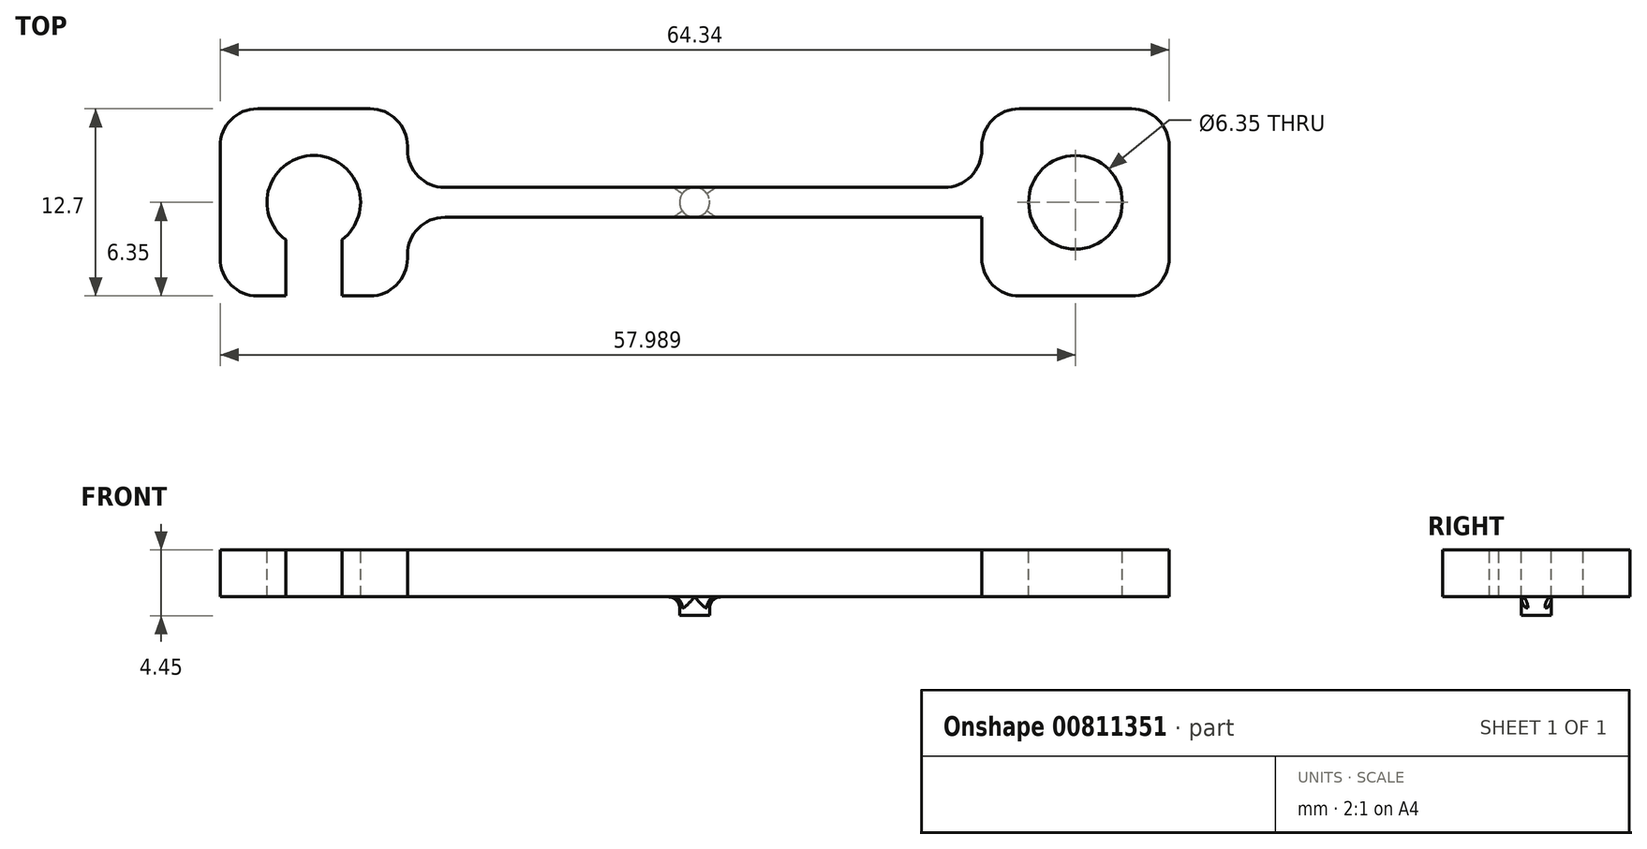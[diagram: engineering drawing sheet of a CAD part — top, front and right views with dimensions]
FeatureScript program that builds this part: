
annotation { "Feature Type Name" : "Feature", "Feature Type Description" : "" }
export const myFeature = defineFeature(function(context is Context, id is Id, definition is map)
    precondition{}
    {
        {
            var Q0;
            Q0=qCreatedBy(makeId("Top.planeOp"),FACE);
            var sketch = newSketch(context, id + "F0", { "sketchPlane" : qUnion([Q0])});
            skLineSegment(sketch, "E0.bottom", {"start": v(32.17, -6.35) * mm, "end": v(19.47, -6.35) * mm});
            skLineSegment(sketch, "E0.top", {"start": v(32.17, 6.35) * mm, "end": v(19.47, 6.35) * mm});
            skLineSegment(sketch, "E0.left", {"start": v(32.17, -6.35) * mm, "end": v(32.17, 6.35) * mm});
            skLineSegment(sketch, "E0.right", {"start": v(-32.17, -6.35) * mm, "end": v(-32.17, 6.35) * mm});
            skPoint(sketch, "E0.middle", {"position": v(0, 0) * mm});
            skLineSegment(sketch, "E1", {"start": v(-19.47, -6.35) * mm, "end": v(-19.47, -1.02) * mm});
            skLineSegment(sketch, "E2", {"start": v(-19.47, -1.02) * mm, "end": v(19.47, -1.02) * mm});
            skLineSegment(sketch, "E3", {"start": v(19.47, -1.02) * mm, "end": v(19.47, -6.35) * mm});
            skLineSegment(sketch, "E4", {"start": v(-19.47, 6.35) * mm, "end": v(-19.47, 1.02) * mm});
            skLineSegment(sketch, "E5", {"start": v(-19.47, 1.02) * mm, "end": v(19.47, 1.02) * mm});
            skLineSegment(sketch, "E6", {"start": v(19.47, 1.02) * mm, "end": v(19.47, 6.35) * mm});
            skLineSegment(sketch, "E7", {"start": v(-32.17, 0) * mm, "end": v(32.17, 0) * mm, "construction": true});
            skLineSegment(sketch, "E8", {"start": v(0, 6.35) * mm, "end": v(0, -6.35) * mm, "construction": true});
            skLineSegment(sketch, "E9.trimOffspring", {"start": v(-19.47, 6.35) * mm, "end": v(-32.17, 6.35) * mm});
            skLineSegment(sketch, "E10.trimOffspring", {"start": v(-19.47, -6.35) * mm, "end": v(-32.17, -6.35) * mm});
            skSolve(sketch);
        }
        {
            var Q0;
            Q0=makeQuery(id+"F0.imprint","IMPRINT",FACE,{"disambiguationData":[TD([[makeQuery(id+"F0.imprint","IMPRINT",EDGE,{"derivedFrom":sQuery(id+"F0.wireOp",EDGE,"E0.bottom")}),-1.0]])]});
            extrude(context, id + "F1", {"entities" : qUnion([Q0]), "oppositeDirection" : true, "depth" : 3.17 * mm, "offsetDistance" : 25.4 * mm});
        }
        {
            var Q0;
            Q0=makeQuery(id+"F1.opExtrude","CAP_FACE",FACE,{"disambiguationData":[OSD([sQuery(id+"F0.wireOp",EDGE,"E0.bottom"),sQuery(id+"F0.wireOp",EDGE,"E0.top"),sQuery(id+"F0.wireOp",EDGE,"E0.left"),sQuery(id+"F0.wireOp",EDGE,"E0.right"),sQuery(id+"F0.wireOp",EDGE,"E1"),sQuery(id+"F0.wireOp",EDGE,"E2"),sQuery(id+"F0.wireOp",EDGE,"E3"),sQuery(id+"F0.wireOp",EDGE,"E4"),sQuery(id+"F0.wireOp",EDGE,"E5"),sQuery(id+"F0.wireOp",EDGE,"E6"),sQuery(id+"F0.wireOp",EDGE,"E9.trimOffspring"),sQuery(id+"F0.wireOp",EDGE,"E10.trimOffspring")])],"isStart":true});
            var sketch = newSketch(context, id + "F2", { "sketchPlane" : qUnion([Q0])});
            skLineSegment(sketch, "E11", {"start": v(0, 1.02) * mm, "end": v(0, -1.02) * mm, "construction": true});
            skCircle(sketch, "E12", {"center": v(-25.82, 0) * mm, "radius": 3.18 * mm});
            skCircle(sketch, "E13", {"center": v(25.82, 0) * mm, "radius": 3.18 * mm});
            skLineSegment(sketch, "E14", {"start": v(-25.82, 6.35) * mm, "end": v(-25.82, -6.35) * mm, "construction": true});
            skSolve(sketch);
        }
        {
            var Q0;
            Q0=makeQuery(id+"F2.imprint","IMPRINT",FACE,{"disambiguationData":[TD([[makeQuery(id+"F2.imprint","IMPRINT",EDGE,{"derivedFrom":sQuery(id+"F2.wireOp",EDGE,"E12")}),1.0]])]});
            var Q1;
            Q1=makeQuery(id+"F2.imprint","IMPRINT",FACE,{"disambiguationData":[TD([[makeQuery(id+"F2.imprint","IMPRINT",EDGE,{"derivedFrom":sQuery(id+"F2.wireOp",EDGE,"E13")}),1.0]])]});
            extrude(context, id + "F3", {"entities" : qUnion([Q0, Q1]), "operationType" : NewBodyOperationType.REMOVE, "endBound" : BoundingType.THROUGH_ALL, "oppositeDirection" : true, "depth" : 25.4 * mm, "offsetDistance" : 25.4 * mm});
        }
        {
            var Q0;
            Q0=makeQuery(id+"F1.opExtrude","CAP_FACE",FACE,{"disambiguationData":[OSD([sQuery(id+"F0.wireOp",EDGE,"E0.bottom"),sQuery(id+"F0.wireOp",EDGE,"E0.top"),sQuery(id+"F0.wireOp",EDGE,"E0.left"),sQuery(id+"F0.wireOp",EDGE,"E0.right"),sQuery(id+"F0.wireOp",EDGE,"E1"),sQuery(id+"F0.wireOp",EDGE,"E2"),sQuery(id+"F0.wireOp",EDGE,"E3"),sQuery(id+"F0.wireOp",EDGE,"E4"),sQuery(id+"F0.wireOp",EDGE,"E5"),sQuery(id+"F0.wireOp",EDGE,"E6"),sQuery(id+"F0.wireOp",EDGE,"E9.trimOffspring"),sQuery(id+"F0.wireOp",EDGE,"E10.trimOffspring")])],"isStart":true});
            var sketch = newSketch(context, id + "F4", { "sketchPlane" : qUnion([Q0])});
            skLineSegment(sketch, "E15", {"start": v(-25.82, 6.35) * mm, "end": v(-25.82, -6.35) * mm, "construction": true});
            skLineSegment(sketch, "E16", {"start": v(-29, 0) * mm, "end": v(-22.64, 0) * mm, "construction": true});
            skLineSegment(sketch, "E17.bottom", {"start": v(-27.72, -6.35) * mm, "end": v(-23.91, -6.35) * mm});
            skLineSegment(sketch, "E17.top", {"start": v(-27.72, 0) * mm, "end": v(-23.91, 0) * mm});
            skLineSegment(sketch, "E17.left", {"start": v(-27.72, -6.35) * mm, "end": v(-27.72, 0) * mm});
            skLineSegment(sketch, "E17.right", {"start": v(-23.91, -6.35) * mm, "end": v(-23.91, 0) * mm});
            skSolve(sketch);
        }
        {
            var Q0;
            {var subQ0=sQuery(id+"F4.wireOp",EDGE,"E17.bottom");Q0=makeQuery(id+"F4.imprint","IMPRINT",FACE,{"disambiguationData":[TD([[makeQuery(id+"F4.imprint","IMPRINT",EDGE,{"derivedFrom":subQ0}),-1.0]])]});}
            extrude(context, id + "F5", {"entities" : qUnion([Q0]), "operationType" : NewBodyOperationType.REMOVE, "endBound" : BoundingType.THROUGH_ALL, "oppositeDirection" : true, "depth" : 25.4 * mm, "offsetDistance" : 25.4 * mm});
        }
        {
            var Q0;
            Q0=makeQuery(id+"F1.opExtrude","CAP_FACE",FACE,{"disambiguationData":[OSD([sQuery(id+"F0.wireOp",EDGE,"E0.bottom"),sQuery(id+"F0.wireOp",EDGE,"E0.top"),sQuery(id+"F0.wireOp",EDGE,"E0.left"),sQuery(id+"F0.wireOp",EDGE,"E0.right"),sQuery(id+"F0.wireOp",EDGE,"E1"),sQuery(id+"F0.wireOp",EDGE,"E2"),sQuery(id+"F0.wireOp",EDGE,"E3"),sQuery(id+"F0.wireOp",EDGE,"E4"),sQuery(id+"F0.wireOp",EDGE,"E5"),sQuery(id+"F0.wireOp",EDGE,"E6"),sQuery(id+"F0.wireOp",EDGE,"E9.trimOffspring"),sQuery(id+"F0.wireOp",EDGE,"E10.trimOffspring")])],"isStart":false});
            var sketch = newSketch(context, id + "F6", { "sketchPlane" : qUnion([Q0])});
            skCircle(sketch, "E18", {"center": v(0, 0) * mm, "radius": 1.02 * mm});
            skSolve(sketch);
        }
        {
            var Q0;
            Q0 = qSketchRegion(id + "F6", true);
            extrude(context, id + "F7", {"entities" : qUnion([Q0]), "operationType" : NewBodyOperationType.ADD, "depth" : 1.27 * mm, "offsetDistance" : 25.4 * mm});
        }
        {
            var Q0;
            Q0=makeQuery(id+"F7.boolean.opBoolean","SPLIT",EDGE,{"disambiguationData":[OD(1.0)],"derivedFrom":makeQuery(id+"F7.opExtrude","CAP_EDGE",EDGE,{"disambiguationData":[OSD([sQuery(id+"F6.wireOp",EDGE,"E18")])],"isStart":true})});
            var Q1;
            Q1=makeQuery(id+"F7.boolean.opBoolean","SPLIT",EDGE,{"disambiguationData":[OD(0.0)],"derivedFrom":makeQuery(id+"F7.opExtrude","CAP_EDGE",EDGE,{"disambiguationData":[OSD([sQuery(id+"F6.wireOp",EDGE,"E18")])],"isStart":true})});
            fillet(context, id + "F8", {"entities" : qUnion([Q0, Q1]), "radius" : 0.76 * mm, "tangentPropagation" : true, "allowEdgeOverflow" : false});
        }
        {
            var Q0;
            Q0=makeQuery(id+"F1.opExtrude","SWEPT_EDGE",EDGE,{"disambiguationData":[OSD([sQuery(id+"F0.wireOp",EDGE,"E1"),sQuery(id+"F0.wireOp",EDGE,"E2")])]});
            var Q1;
            Q1=makeQuery(id+"F1.opExtrude","SWEPT_EDGE",EDGE,{"disambiguationData":[OSD([sQuery(id+"F0.wireOp",EDGE,"E1"),sQuery(id+"F0.wireOp",EDGE,"E10.trimOffspring")])]});
            var Q2;
            Q2=makeQuery(id+"F1.opExtrude","SWEPT_EDGE",EDGE,{"disambiguationData":[OSD([sQuery(id+"F0.wireOp",EDGE,"E0.right"),sQuery(id+"F0.wireOp",EDGE,"E10.trimOffspring")])]});
            var Q3;
            Q3=makeQuery(id+"F1.opExtrude","SWEPT_EDGE",EDGE,{"disambiguationData":[OSD([sQuery(id+"F0.wireOp",EDGE,"E0.right"),sQuery(id+"F0.wireOp",EDGE,"E9.trimOffspring")])]});
            var Q4;
            Q4=makeQuery(id+"F1.opExtrude","SWEPT_EDGE",EDGE,{"disambiguationData":[OSD([sQuery(id+"F0.wireOp",EDGE,"E4"),sQuery(id+"F0.wireOp",EDGE,"E9.trimOffspring")])]});
            var Q5;
            Q5=makeQuery(id+"F1.opExtrude","SWEPT_EDGE",EDGE,{"disambiguationData":[OSD([sQuery(id+"F0.wireOp",EDGE,"E4"),sQuery(id+"F0.wireOp",EDGE,"E5")])]});
            var Q6;
            Q6=makeQuery(id+"F1.opExtrude","SWEPT_EDGE",EDGE,{"disambiguationData":[OSD([sQuery(id+"F0.wireOp",EDGE,"E5"),sQuery(id+"F0.wireOp",EDGE,"E6")])]});
            var Q7;
            Q7=makeQuery(id+"F1.opExtrude","SWEPT_EDGE",EDGE,{"disambiguationData":[OSD([sQuery(id+"F0.wireOp",EDGE,"E0.top"),sQuery(id+"F0.wireOp",EDGE,"E6")])]});
            var Q8;
            Q8=makeQuery(id+"F1.opExtrude","SWEPT_EDGE",EDGE,{"disambiguationData":[OSD([sQuery(id+"F0.wireOp",EDGE,"E0.top"),sQuery(id+"F0.wireOp",EDGE,"E0.left")])]});
            var Q9;
            Q9=makeQuery(id+"F1.opExtrude","SWEPT_EDGE",EDGE,{"disambiguationData":[OSD([sQuery(id+"F0.wireOp",EDGE,"E0.bottom"),sQuery(id+"F0.wireOp",EDGE,"E3")])]});
            var Q10;
            Q10=makeQuery(id+"F1.opExtrude","SWEPT_EDGE",EDGE,{"disambiguationData":[OSD([sQuery(id+"F0.wireOp",EDGE,"E0.bottom"),sQuery(id+"F0.wireOp",EDGE,"E0.left")])]});
            fillet(context, id + "F9", {"entities" : qUnion([Q0, Q1, Q2, Q3, Q4, Q5, Q6, Q7, Q8, Q9, Q10]), "radius" : 2.54 * mm, "tangentPropagation" : true, "allowEdgeOverflow" : false});
        }
    });
